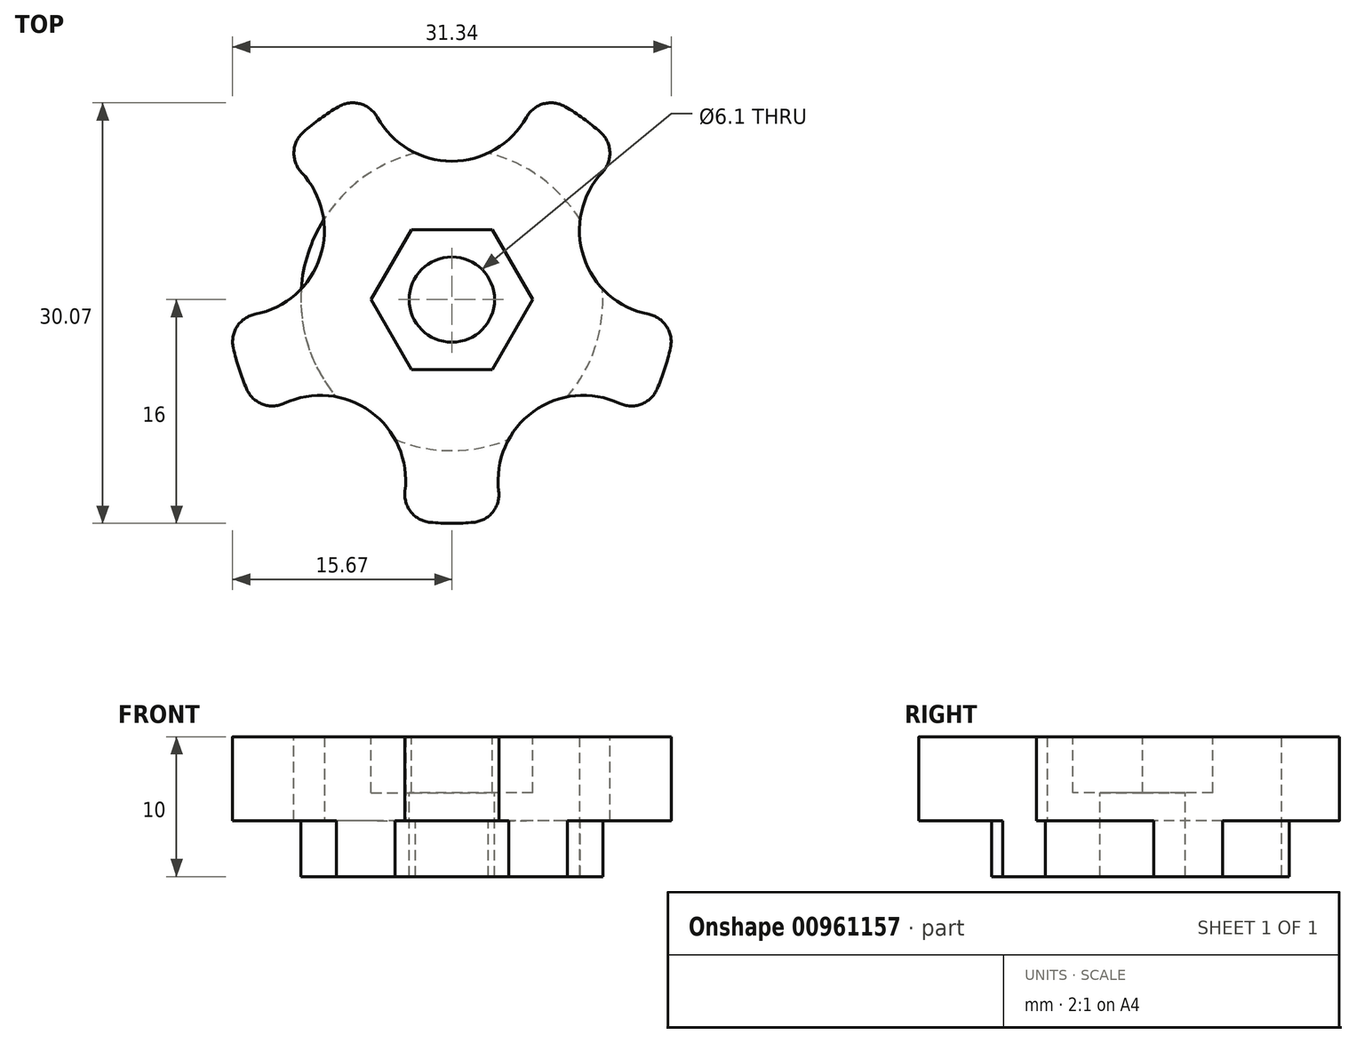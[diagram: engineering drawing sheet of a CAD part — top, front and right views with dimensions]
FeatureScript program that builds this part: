
annotation { "Feature Type Name" : "Feature", "Feature Type Description" : "" }
export const myFeature = defineFeature(function(context is Context, id is Id, definition is map)
    precondition{}
    {
        {
            var Q0;
            Q0=qCreatedBy(makeId("Top.planeOp"),FACE);
            var sketch = newSketch(context, id + "F0", { "sketchPlane" : qUnion([Q0])});
            skCircle(sketch, "E0", {"center": v(0, 0) * mm, "radius": 10.8 * mm});
            skSolve(sketch);
        }
        {
            var Q0;
            Q0=makeQuery(id+"F0.imprint","IMPRINT",FACE,{"disambiguationData":[TD([[makeQuery(id+"F0.imprint","IMPRINT",EDGE,{"derivedFrom":sQuery(id+"F0.wireOp",EDGE,"E0")}),1.0]])]});
            extrude(context, id + "F1", {"entities" : qUnion([Q0]), "depth" : 4 * mm, "offsetDistance" : 25 * mm});
        }
        {
            var Q0;
            Q0=makeQuery(id+"F1.opExtrude","CAP_FACE",FACE,{"disambiguationData":[OSD([sQuery(id+"F0.wireOp",EDGE,"E0")])],"isStart":false});
            var sketch = newSketch(context, id + "F2", { "sketchPlane" : qUnion([Q0])});
            skCircle(sketch, "E1", {"center": v(0, 0) * mm, "radius": 16 * mm});
            skCircle(sketch, "E2", {"center": v(0, 16) * mm, "radius": 6.1 * mm});
            skCircle(sketch, "E3.1.0", {"center": v(-15.22, 4.94) * mm, "radius": 6.1 * mm});
            skCircle(sketch, "E3.2.0", {"center": v(-9.4, -12.94) * mm, "radius": 6.1 * mm});
            skCircle(sketch, "E3.3.0", {"center": v(9.4, -12.94) * mm, "radius": 6.1 * mm});
            skCircle(sketch, "E3.4.0", {"center": v(15.22, 4.94) * mm, "radius": 6.1 * mm});
            skSolve(sketch);
        }
        {
            var Q0;
            Q0=makeQuery(id+"F2.imprint","IMPRINT",FACE,{"disambiguationData":[TD([[makeQuery(id+"F2.imprint","IMPRINT",EDGE,{"derivedFrom":makeQuery(id+"F1.opExtrude","CAP_EDGE",EDGE,{"disambiguationData":[OSD([sQuery(id+"F0.wireOp",EDGE,"E0")])],"isStart":false})}),1.0]])]});
            var Q1;
            {var subQ0=sQuery(id+"F2.wireOp",EDGE,"E2");var subQ1=sQuery(id+"F2.wireOp",EDGE,"E1");var subQ2=makeQuery(id+"F2.imprint","INTERSECT",VERTEX,{"disambiguationData":[OD(0.0)],"derivedFrom":[subQ1,subQ0]});Q1=makeQuery(id+"F2.imprint","IMPRINT",FACE,{"disambiguationData":[TD([[makeQuery(id+"F2.imprint","IMPRINT",EDGE,{"disambiguationData":[TD([[subQ2,1.0]])],"derivedFrom":subQ1}),1.0]])]});}
            var Q2;
            {var subQ0=sQuery(id+"F2.wireOp",EDGE,"E2");var subQ1=sQuery(id+"F2.wireOp",EDGE,"E1");var subQ2=makeQuery(id+"F2.imprint","INTERSECT",VERTEX,{"disambiguationData":[OD(1.0)],"derivedFrom":[subQ1,subQ0]});Q2=makeQuery(id+"F2.imprint","IMPRINT",FACE,{"disambiguationData":[TD([[makeQuery(id+"F2.imprint","IMPRINT",EDGE,{"disambiguationData":[TD([[subQ2,-1.0]])],"derivedFrom":subQ1}),1.0]])]});}
            var Q3;
            {var subQ0=sQuery(id+"F2.wireOp",EDGE,"E3.1.0");var subQ1=sQuery(id+"F2.wireOp",EDGE,"E1");var subQ2=makeQuery(id+"F2.imprint","INTERSECT",VERTEX,{"disambiguationData":[OD(1.0)],"derivedFrom":[subQ1,subQ0]});Q3=makeQuery(id+"F2.imprint","IMPRINT",FACE,{"disambiguationData":[TD([[makeQuery(id+"F2.imprint","IMPRINT",EDGE,{"disambiguationData":[TD([[subQ2,-1.0]])],"derivedFrom":subQ1}),1.0]])]});}
            var Q4;
            {var subQ0=sQuery(id+"F2.wireOp",EDGE,"E3.2.0");var subQ1=sQuery(id+"F2.wireOp",EDGE,"E1");var subQ2=makeQuery(id+"F2.imprint","INTERSECT",VERTEX,{"disambiguationData":[OD(1.0)],"derivedFrom":[subQ1,subQ0]});Q4=makeQuery(id+"F2.imprint","IMPRINT",FACE,{"disambiguationData":[TD([[makeQuery(id+"F2.imprint","IMPRINT",EDGE,{"disambiguationData":[TD([[subQ2,-1.0]])],"derivedFrom":subQ1}),1.0]])]});}
            var Q5;
            {var subQ0=sQuery(id+"F2.wireOp",EDGE,"E3.3.0");var subQ1=sQuery(id+"F2.wireOp",EDGE,"E1");var subQ2=makeQuery(id+"F2.imprint","INTERSECT",VERTEX,{"disambiguationData":[OD(1.0)],"derivedFrom":[subQ1,subQ0]});Q5=makeQuery(id+"F2.imprint","IMPRINT",FACE,{"disambiguationData":[TD([[makeQuery(id+"F2.imprint","IMPRINT",EDGE,{"disambiguationData":[TD([[subQ2,-1.0]])],"derivedFrom":subQ1}),1.0]])]});}
            extrude(context, id + "F3", {"entities" : qUnion([Q0, Q1, Q2, Q3, Q4, Q5]), "operationType" : NewBodyOperationType.ADD, "depth" : 6 * mm, "offsetDistance" : 25 * mm});
        }
        {
            var Q0;
            {var subQ0=sQuery(id+"F2.wireOp",EDGE,"E2");var subQ1=sQuery(id+"F2.wireOp",EDGE,"E1");Q0=makeQuery(id+"F3.opExtrude","SWEPT_EDGE",EDGE,{"disambiguationData":[OSD([subQ1,subQ0]),TDD([makeQuery(id+"F2.imprint","INTERSECT",VERTEX,{"disambiguationData":[OD(1.0)],"derivedFrom":[subQ1,subQ0]})])]});}
            var Q1;
            {var subQ0=sQuery(id+"F2.wireOp",EDGE,"E3.1.0");var subQ1=sQuery(id+"F2.wireOp",EDGE,"E1");Q1=makeQuery(id+"F3.opExtrude","SWEPT_EDGE",EDGE,{"disambiguationData":[OSD([subQ1,subQ0]),TDD([makeQuery(id+"F2.imprint","INTERSECT",VERTEX,{"disambiguationData":[OD(0.0)],"derivedFrom":[subQ1,subQ0]})])]});}
            var Q2;
            {var subQ0=sQuery(id+"F2.wireOp",EDGE,"E3.1.0");var subQ1=sQuery(id+"F2.wireOp",EDGE,"E1");Q2=makeQuery(id+"F3.opExtrude","SWEPT_EDGE",EDGE,{"disambiguationData":[OSD([subQ1,subQ0]),TDD([makeQuery(id+"F2.imprint","INTERSECT",VERTEX,{"disambiguationData":[OD(1.0)],"derivedFrom":[subQ1,subQ0]})])]});}
            var Q3;
            {var subQ0=sQuery(id+"F2.wireOp",EDGE,"E3.2.0");var subQ1=sQuery(id+"F2.wireOp",EDGE,"E1");Q3=makeQuery(id+"F3.opExtrude","SWEPT_EDGE",EDGE,{"disambiguationData":[OSD([subQ1,subQ0]),TDD([makeQuery(id+"F2.imprint","INTERSECT",VERTEX,{"disambiguationData":[OD(0.0)],"derivedFrom":[subQ1,subQ0]})])]});}
            var Q4;
            {var subQ0=sQuery(id+"F2.wireOp",EDGE,"E3.2.0");var subQ1=sQuery(id+"F2.wireOp",EDGE,"E1");Q4=makeQuery(id+"F3.opExtrude","SWEPT_EDGE",EDGE,{"disambiguationData":[OSD([subQ1,subQ0]),TDD([makeQuery(id+"F2.imprint","INTERSECT",VERTEX,{"disambiguationData":[OD(1.0)],"derivedFrom":[subQ1,subQ0]})])]});}
            var Q5;
            {var subQ0=sQuery(id+"F2.wireOp",EDGE,"E3.3.0");var subQ1=sQuery(id+"F2.wireOp",EDGE,"E1");Q5=makeQuery(id+"F3.opExtrude","SWEPT_EDGE",EDGE,{"disambiguationData":[OSD([subQ1,subQ0]),TDD([makeQuery(id+"F2.imprint","INTERSECT",VERTEX,{"disambiguationData":[OD(0.0)],"derivedFrom":[subQ1,subQ0]})])]});}
            var Q6;
            {var subQ0=sQuery(id+"F2.wireOp",EDGE,"E3.3.0");var subQ1=sQuery(id+"F2.wireOp",EDGE,"E1");Q6=makeQuery(id+"F3.opExtrude","SWEPT_EDGE",EDGE,{"disambiguationData":[OSD([subQ1,subQ0]),TDD([makeQuery(id+"F2.imprint","INTERSECT",VERTEX,{"disambiguationData":[OD(1.0)],"derivedFrom":[subQ1,subQ0]})])]});}
            var Q7;
            {var subQ0=sQuery(id+"F2.wireOp",EDGE,"E3.4.0");var subQ1=sQuery(id+"F2.wireOp",EDGE,"E1");Q7=makeQuery(id+"F3.opExtrude","SWEPT_EDGE",EDGE,{"disambiguationData":[OSD([subQ1,subQ0]),TDD([makeQuery(id+"F2.imprint","INTERSECT",VERTEX,{"disambiguationData":[OD(1.0)],"derivedFrom":[subQ1,subQ0]})])]});}
            var Q8;
            {var subQ0=sQuery(id+"F2.wireOp",EDGE,"E3.4.0");var subQ1=sQuery(id+"F2.wireOp",EDGE,"E1");Q8=makeQuery(id+"F3.opExtrude","SWEPT_EDGE",EDGE,{"disambiguationData":[OSD([subQ1,subQ0]),TDD([makeQuery(id+"F2.imprint","INTERSECT",VERTEX,{"disambiguationData":[OD(0.0)],"derivedFrom":[subQ1,subQ0]})])]});}
            var Q9;
            {var subQ0=sQuery(id+"F2.wireOp",EDGE,"E2");var subQ1=sQuery(id+"F2.wireOp",EDGE,"E1");Q9=makeQuery(id+"F3.opExtrude","SWEPT_EDGE",EDGE,{"disambiguationData":[OSD([subQ1,subQ0]),TDD([makeQuery(id+"F2.imprint","INTERSECT",VERTEX,{"disambiguationData":[OD(0.0)],"derivedFrom":[subQ1,subQ0]})])]});}
            fillet(context, id + "F4", {"entities" : qUnion([Q0, Q1, Q2, Q3, Q4, Q5, Q6, Q7, Q8, Q9]), "radius" : 2 * mm, "tangentPropagation" : true, "allowEdgeOverflow" : false});
        }
        {
            var Q0;
            Q0=makeQuery(id+"F3.opExtrude","CAP_FACE",FACE,{"disambiguationData":[OSD([sQuery(id+"F2.wireOp",EDGE,"E1"),sQuery(id+"F2.wireOp",EDGE,"E2"),sQuery(id+"F2.wireOp",EDGE,"E3.1.0"),sQuery(id+"F2.wireOp",EDGE,"E3.2.0"),sQuery(id+"F2.wireOp",EDGE,"E3.3.0"),sQuery(id+"F2.wireOp",EDGE,"E3.4.0")])],"isStart":false});
            var sketch = newSketch(context, id + "F5", { "sketchPlane" : qUnion([Q0])});
            skCircle(sketch, "E4", {"center": v(0, 0) * mm, "radius": 3.05 * mm});
            skSolve(sketch);
        }
        {
            var Q0;
            Q0=qSketchRegion(id+"F5",true);
            extrude(context, id + "F6", {"entities" : qUnion([Q0]), "operationType" : NewBodyOperationType.REMOVE, "oppositeDirection" : true, "depth" : 25 * mm, "offsetDistance" : 25 * mm});
        }
        {
            var Q0;
            Q0=makeQuery(id+"F3.opExtrude","CAP_FACE",FACE,{"disambiguationData":[OSD([sQuery(id+"F2.wireOp",EDGE,"E1"),sQuery(id+"F2.wireOp",EDGE,"E2"),sQuery(id+"F2.wireOp",EDGE,"E3.1.0"),sQuery(id+"F2.wireOp",EDGE,"E3.2.0"),sQuery(id+"F2.wireOp",EDGE,"E3.3.0"),sQuery(id+"F2.wireOp",EDGE,"E3.4.0")])],"isStart":false});
            var sketch = newSketch(context, id + "F7", { "sketchPlane" : qUnion([Q0])});
            skCircle(sketch, "E5.cCircle", {"center": v(0, 0) * mm, "radius": 5 * mm, "construction": true});
            skLineSegment(sketch, "E5.0", {"start": v(5.77, 0) * mm, "end": v(2.89, -5) * mm});
            skLineSegment(sketch, "E5.1", {"start": v(2.89, -5) * mm, "end": v(-2.89, -5) * mm});
            skLineSegment(sketch, "E5.2", {"start": v(-2.89, -5) * mm, "end": v(-5.77, 0) * mm});
            skLineSegment(sketch, "E5.3", {"start": v(-5.77, 0) * mm, "end": v(-2.89, 5) * mm});
            skLineSegment(sketch, "E5.4", {"start": v(-2.89, 5) * mm, "end": v(2.89, 5) * mm});
            skLineSegment(sketch, "E5.5", {"start": v(2.89, 5) * mm, "end": v(5.77, 0) * mm});
            skPoint(sketch, "E5.0.midPoint", {"position": v(4.33, -2.5) * mm});
            skSolve(sketch);
        }
        {
            var Q0;
            Q0=qSketchRegion(id+"F7",true);
            extrude(context, id + "F8", {"entities" : qUnion([Q0]), "operationType" : NewBodyOperationType.REMOVE, "oppositeDirection" : true, "depth" : 4 * mm, "offsetDistance" : 25 * mm});
        }
        {
            var Q0;
            {var subQ0=sQuery(id+"F2.wireOp",EDGE,"E3.1.0");var subQ1=makeQuery(id+"F1.opExtrude","CAP_EDGE",EDGE,{"disambiguationData":[OSD([sQuery(id+"F0.wireOp",EDGE,"E0")])],"isStart":false});var subQ2=makeQuery(id+"F2.imprint","INTERSECT",VERTEX,{"disambiguationData":[OD(0.0)],"derivedFrom":[subQ1,subQ0]});Q0=makeQuery(id+"F2.imprint","IMPRINT",FACE,{"disambiguationData":[TD([[makeQuery(id+"F2.imprint","IMPRINT",EDGE,{"disambiguationData":[TD([[subQ2,-1.0]])],"derivedFrom":subQ0}),1.0]])]});}
            var Q1;
            {var subQ0=sQuery(id+"F2.wireOp",EDGE,"E2");var subQ1=makeQuery(id+"F1.opExtrude","CAP_EDGE",EDGE,{"disambiguationData":[OSD([sQuery(id+"F0.wireOp",EDGE,"E0")])],"isStart":false});var subQ2=makeQuery(id+"F2.imprint","INTERSECT",VERTEX,{"disambiguationData":[OD(0.0)],"derivedFrom":[subQ1,subQ0]});Q1=makeQuery(id+"F2.imprint","IMPRINT",FACE,{"disambiguationData":[TD([[makeQuery(id+"F2.imprint","IMPRINT",EDGE,{"disambiguationData":[TD([[subQ2,-1.0]])],"derivedFrom":subQ0}),1.0]])]});}
            var Q2;
            {var subQ0=sQuery(id+"F2.wireOp",EDGE,"E3.4.0");var subQ1=makeQuery(id+"F1.opExtrude","CAP_EDGE",EDGE,{"disambiguationData":[OSD([sQuery(id+"F0.wireOp",EDGE,"E0")])],"isStart":false});var subQ2=makeQuery(id+"F2.imprint","INTERSECT",VERTEX,{"disambiguationData":[OD(0.0)],"derivedFrom":[subQ1,subQ0]});Q2=makeQuery(id+"F2.imprint","IMPRINT",FACE,{"disambiguationData":[TD([[makeQuery(id+"F2.imprint","IMPRINT",EDGE,{"disambiguationData":[TD([[subQ2,-1.0]])],"derivedFrom":subQ0}),1.0]])]});}
            var Q3;
            {var subQ0=sQuery(id+"F2.wireOp",EDGE,"E3.3.0");var subQ1=makeQuery(id+"F1.opExtrude","CAP_EDGE",EDGE,{"disambiguationData":[OSD([sQuery(id+"F0.wireOp",EDGE,"E0")])],"isStart":false});var subQ2=makeQuery(id+"F2.imprint","INTERSECT",VERTEX,{"disambiguationData":[OD(0.0)],"derivedFrom":[subQ1,subQ0]});Q3=makeQuery(id+"F2.imprint","IMPRINT",FACE,{"disambiguationData":[TD([[makeQuery(id+"F2.imprint","IMPRINT",EDGE,{"disambiguationData":[TD([[subQ2,-1.0]])],"derivedFrom":subQ0}),1.0]])]});}
            var Q4;
            {var subQ0=sQuery(id+"F2.wireOp",EDGE,"E3.2.0");var subQ1=makeQuery(id+"F1.opExtrude","CAP_EDGE",EDGE,{"disambiguationData":[OSD([sQuery(id+"F0.wireOp",EDGE,"E0")])],"isStart":false});var subQ2=makeQuery(id+"F2.imprint","INTERSECT",VERTEX,{"disambiguationData":[OD(0.0)],"derivedFrom":[subQ1,subQ0]});Q4=makeQuery(id+"F2.imprint","IMPRINT",FACE,{"disambiguationData":[TD([[makeQuery(id+"F2.imprint","IMPRINT",EDGE,{"disambiguationData":[TD([[subQ2,-1.0]])],"derivedFrom":subQ0}),1.0]])]});}
            extrude(context, id + "F9", {"entities" : qUnion([Q0, Q1, Q2, Q3, Q4]), "operationType" : NewBodyOperationType.REMOVE, "oppositeDirection" : true, "depth" : 25 * mm, "offsetDistance" : 25 * mm});
        }
    });
